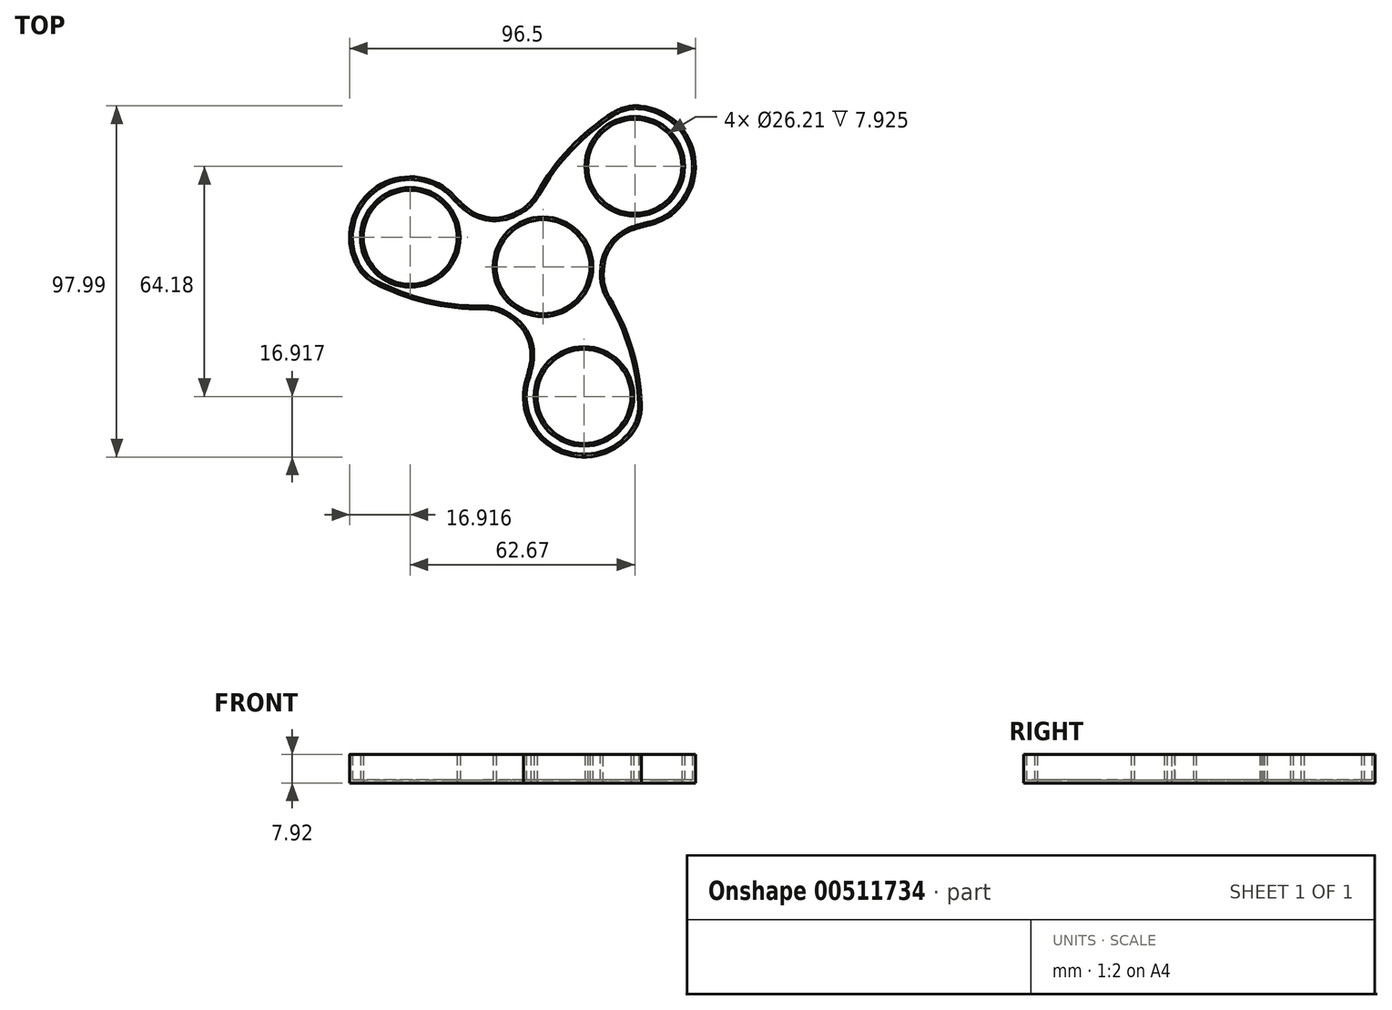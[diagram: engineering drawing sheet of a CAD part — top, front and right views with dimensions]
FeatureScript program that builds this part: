
annotation { "Feature Type Name" : "Feature", "Feature Type Description" : "" }
export const myFeature = defineFeature(function(context is Context, id is Id, definition is map)
    precondition{}
    {
        {
            var Q0;
            Q0=qCreatedBy(makeId("Top.planeOp"),FACE);
            var sketch = newSketch(context, id + "F0", { "sketchPlane" : qUnion([Q0])});
            skCircle(sketch, "E0", {"center": v(21.35, 23.33) * mm, "radius": 10.92 * mm});
            skCircle(sketch, "E1", {"center": v(0, 0) * mm, "radius": 10.92 * mm});
            skCircle(sketch, "E2", {"center": v(0, 0) * mm, "radius": 45.72 * mm, "construction": true});
            skArc(sketch, "E3", {"start": v(-3.15, 13.74) * mm, "mid": v(-6.74, -12.38) * mm, "end": v(13.25, 4.82) * mm});
            skArc(sketch, "E4", {"start": v(25.57, 9.88) * mm, "mid": v(34.98, 26.9) * mm, "end": v(18.44, 37.12) * mm});
            skArc(sketch, "E5", {"start": v(18.44, 37.12) * mm, "mid": v(5.82, 27.12) * mm, "end": v(-3.15, 13.74) * mm});
            skArc(sketch, "E6", {"start": v(25.57, 9.88) * mm, "mid": v(19.16, 7.94) * mm, "end": v(13.25, 4.82) * mm});
            skSolve(sketch);
        }
        {
            var Q0;
            Q0 = qSketchRegion(id + "F0", true);
            extrude(context, id + "F1", {"entities" : qUnion([Q0]), "depth" : 6.6 * mm});
        }
        {
            var Q0;
            Q0=makeQuery(id+"F1.opExtrude","SWEPT_BODY",BODY,{"disambiguationData":[OSD([sQuery(id+"F0.wireOp",EDGE,"E0"),sQuery(id+"F0.wireOp",EDGE,"E1"),sQuery(id+"F0.wireOp",EDGE,"E3"),sQuery(id+"F0.wireOp",EDGE,"E4"),sQuery(id+"F0.wireOp",EDGE,"E5"),sQuery(id+"F0.wireOp",EDGE,"E6")])]});
            var Q1;
            Q1=makeQuery(id+"F1.opExtrude","CAP_EDGE",EDGE,{"disambiguationData":[OSD([sQuery(id+"F0.wireOp",EDGE,"E1")])],"isStart":false});
            circularPattern(context, id + "F2", {"entities" : qUnion([Q0]), "axis" : qUnion([Q1]), "angle" : 360 * degree, "instanceCount" : 3, "equalSpace" : true});
        }
        {
            var Q0;
            Q0=makeQuery(id+"F2.opPattern","COPY",BODY,{"derivedFrom":makeQuery(id+"F1.opExtrude","SWEPT_BODY",BODY,{"disambiguationData":[OSD([sQuery(id+"F0.wireOp",EDGE,"E0"),sQuery(id+"F0.wireOp",EDGE,"E1"),sQuery(id+"F0.wireOp",EDGE,"E3"),sQuery(id+"F0.wireOp",EDGE,"E4"),sQuery(id+"F0.wireOp",EDGE,"E5"),sQuery(id+"F0.wireOp",EDGE,"E6")])]}),"instanceName":"2"});
            var Q1;
            Q1=makeQuery(id+"F1.opExtrude","SWEPT_BODY",BODY,{"disambiguationData":[OSD([sQuery(id+"F0.wireOp",EDGE,"E0"),sQuery(id+"F0.wireOp",EDGE,"E1"),sQuery(id+"F0.wireOp",EDGE,"E3"),sQuery(id+"F0.wireOp",EDGE,"E4"),sQuery(id+"F0.wireOp",EDGE,"E5"),sQuery(id+"F0.wireOp",EDGE,"E6")])]});
            var Q2;
            Q2=makeQuery(id+"F2.opPattern","COPY",BODY,{"derivedFrom":makeQuery(id+"F1.opExtrude","SWEPT_BODY",BODY,{"disambiguationData":[OSD([sQuery(id+"F0.wireOp",EDGE,"E0"),sQuery(id+"F0.wireOp",EDGE,"E1"),sQuery(id+"F0.wireOp",EDGE,"E3"),sQuery(id+"F0.wireOp",EDGE,"E4"),sQuery(id+"F0.wireOp",EDGE,"E5"),sQuery(id+"F0.wireOp",EDGE,"E6")])]}),"instanceName":"1"});
            booleanBodies(context, id + "F3", {"operationType" : BooleanOperationType.UNION, "tools" : qUnion([Q0, Q1, Q2])});
        }
        {
            var Q0;
            {var subQ0=makeQuery(id+"F1.opExtrude","SWEPT_FACE",FACE,{"disambiguationData":[OSD([sQuery(id+"F0.wireOp",EDGE,"E3")])]});var subQ1=makeQuery(id+"F2.opPattern","COPY",FACE,{"derivedFrom":subQ0,"instanceName":"2"});Q0=makeQuery(id+"F3.opBoolean","INTERSECT",EDGE,{"disambiguationData":[topologyDisambiguationEdgeConnected([makeQuery(id+"F1.opExtrude","SWEPT_FACE",FACE,{"disambiguationData":[OSD([sQuery(id+"F0.wireOp",EDGE,"E5")])]})])],"derivedFrom":[makeQuery(id+"F2.opPattern","COPY",FACE,{"derivedFrom":subQ0,"instanceName":"1"}),subQ1]});}
            var Q1;
            {var subQ0=makeQuery(id+"F1.opExtrude","SWEPT_FACE",FACE,{"disambiguationData":[OSD([sQuery(id+"F0.wireOp",EDGE,"E3")])]});var subQ1=makeQuery(id+"F2.opPattern","COPY",FACE,{"derivedFrom":subQ0,"instanceName":"2"});Q1=makeQuery(id+"F3.opBoolean","INTERSECT",EDGE,{"disambiguationData":[topologyDisambiguationEdgeConnected([makeQuery(id+"F2.opPattern","COPY",FACE,{"derivedFrom":makeQuery(id+"F1.opExtrude","SWEPT_FACE",FACE,{"disambiguationData":[OSD([sQuery(id+"F0.wireOp",EDGE,"E6")])]}),"instanceName":"1"})])],"derivedFrom":[subQ0,subQ1]});}
            var Q2;
            Q2=makeQuery(id+"F1.opExtrude","SWEPT_EDGE",EDGE,{"disambiguationData":[OSD([sQuery(id+"F0.wireOp",EDGE,"E4"),sQuery(id+"F0.wireOp",EDGE,"E5")])]});
            var Q3;
            Q3=makeQuery(id+"F2.opPattern","COPY",EDGE,{"derivedFrom":makeQuery(id+"F1.opExtrude","SWEPT_EDGE",EDGE,{"disambiguationData":[OSD([sQuery(id+"F0.wireOp",EDGE,"E4"),sQuery(id+"F0.wireOp",EDGE,"E6")])]}),"instanceName":"1"});
            var Q4;
            Q4=makeQuery(id+"F1.opExtrude","SWEPT_EDGE",EDGE,{"disambiguationData":[OSD([sQuery(id+"F0.wireOp",EDGE,"E4"),sQuery(id+"F0.wireOp",EDGE,"E6")])]});
            var Q5;
            {var subQ0=makeQuery(id+"F1.opExtrude","SWEPT_FACE",FACE,{"disambiguationData":[OSD([sQuery(id+"F0.wireOp",EDGE,"E3")])]});var subQ1=makeQuery(id+"F2.opPattern","COPY",FACE,{"derivedFrom":subQ0,"instanceName":"2"});Q5=makeQuery(id+"F3.opBoolean","INTERSECT",EDGE,{"disambiguationData":[topologyDisambiguationEdgeConnected([makeQuery(id+"F1.opExtrude","SWEPT_FACE",FACE,{"disambiguationData":[OSD([sQuery(id+"F0.wireOp",EDGE,"E6")])]})])],"derivedFrom":[makeQuery(id+"F2.opPattern","COPY",FACE,{"derivedFrom":subQ0,"instanceName":"1"}),subQ1]});}
            var Q6;
            Q6=makeQuery(id+"F2.opPattern","COPY",EDGE,{"derivedFrom":makeQuery(id+"F1.opExtrude","SWEPT_EDGE",EDGE,{"disambiguationData":[OSD([sQuery(id+"F0.wireOp",EDGE,"E3"),sQuery(id+"F0.wireOp",EDGE,"E5")])]}),"instanceName":"2"});
            var Q7;
            Q7=makeQuery(id+"F2.opPattern","COPY",EDGE,{"derivedFrom":makeQuery(id+"F1.opExtrude","SWEPT_EDGE",EDGE,{"disambiguationData":[OSD([sQuery(id+"F0.wireOp",EDGE,"E4"),sQuery(id+"F0.wireOp",EDGE,"E5")])]}),"instanceName":"2"});
            var Q8;
            Q8=makeQuery(id+"F2.opPattern","COPY",EDGE,{"derivedFrom":makeQuery(id+"F1.opExtrude","SWEPT_EDGE",EDGE,{"disambiguationData":[OSD([sQuery(id+"F0.wireOp",EDGE,"E4"),sQuery(id+"F0.wireOp",EDGE,"E6")])]}),"instanceName":"2"});
            var Q9;
            Q9=makeQuery(id+"F2.opPattern","COPY",EDGE,{"derivedFrom":makeQuery(id+"F1.opExtrude","SWEPT_EDGE",EDGE,{"disambiguationData":[OSD([sQuery(id+"F0.wireOp",EDGE,"E3"),sQuery(id+"F0.wireOp",EDGE,"E6")])]}),"instanceName":"2"});
            var Q10;
            {var subQ0=makeQuery(id+"F1.opExtrude","SWEPT_FACE",FACE,{"disambiguationData":[OSD([sQuery(id+"F0.wireOp",EDGE,"E3")])]});var subQ1=makeQuery(id+"F2.opPattern","COPY",FACE,{"derivedFrom":subQ0,"instanceName":"2"});Q10=makeQuery(id+"F3.opBoolean","INTERSECT",EDGE,{"disambiguationData":[topologyDisambiguationEdgeConnected([makeQuery(id+"F2.opPattern","COPY",FACE,{"derivedFrom":makeQuery(id+"F1.opExtrude","SWEPT_FACE",FACE,{"disambiguationData":[OSD([sQuery(id+"F0.wireOp",EDGE,"E5")])]}),"instanceName":"1"})])],"derivedFrom":[subQ0,subQ1]});}
            var Q11;
            Q11=makeQuery(id+"F2.opPattern","COPY",EDGE,{"derivedFrom":makeQuery(id+"F1.opExtrude","SWEPT_EDGE",EDGE,{"disambiguationData":[OSD([sQuery(id+"F0.wireOp",EDGE,"E4"),sQuery(id+"F0.wireOp",EDGE,"E5")])]}),"instanceName":"1"});
            fillet(context, id + "F4", {"entities" : qUnion([Q0, Q1, Q2, Q3, Q4, Q5, Q6, Q7, Q8, Q9, Q10, Q11]), "radius" : 10.16 * mm, "tangentPropagation" : true, "allowEdgeOverflow" : false});
        }
        {
            var Q0;
            Q0=makeQuery(id+"F2.opPattern","COPY",BODY,{"derivedFrom":makeQuery(id+"F1.opExtrude","SWEPT_BODY",BODY,{"disambiguationData":[OSD([sQuery(id+"F0.wireOp",EDGE,"E0"),sQuery(id+"F0.wireOp",EDGE,"E1"),sQuery(id+"F0.wireOp",EDGE,"E3"),sQuery(id+"F0.wireOp",EDGE,"E4"),sQuery(id+"F0.wireOp",EDGE,"E5"),sQuery(id+"F0.wireOp",EDGE,"E6")])]}),"instanceName":"2"});
            var Q1;
            Q1=qCreatedBy(makeId("Origin.pointOp"),VERTEX);
            var Q2;
            Q2=qCreatedBy(makeId("Origin.pointOp"),VERTEX);
            transform(context, id + "F5", {"entities" : qUnion([Q0]), "transformType" : TransformType.SCALE_UNIFORMLY, "scale" : 1.2, "scalePoint" : qUnion([Q2]), "makeCopy" : false});
        }
        {
            var Q0;
            {var subQ0=makeQuery(id+"F1.opExtrude","CAP_FACE",FACE,{"disambiguationData":[OSD([sQuery(id+"F0.wireOp",EDGE,"E0"),sQuery(id+"F0.wireOp",EDGE,"E1"),sQuery(id+"F0.wireOp",EDGE,"E3"),sQuery(id+"F0.wireOp",EDGE,"E4"),sQuery(id+"F0.wireOp",EDGE,"E5"),sQuery(id+"F0.wireOp",EDGE,"E6")])],"isStart":false});Q0=makeQuery(id+"F3.opBoolean","MERGE",FACE,{"derivedFrom":[subQ0,makeQuery(id+"F2.opPattern","COPY",FACE,{"derivedFrom":subQ0,"instanceName":"1"}),makeQuery(id+"F2.opPattern","COPY",FACE,{"derivedFrom":subQ0,"instanceName":"2"})]});}
            shell(context, id + "F6", {"entities" : qUnion([Q0]), "thickness" : .8 * mm});
        }
    });
